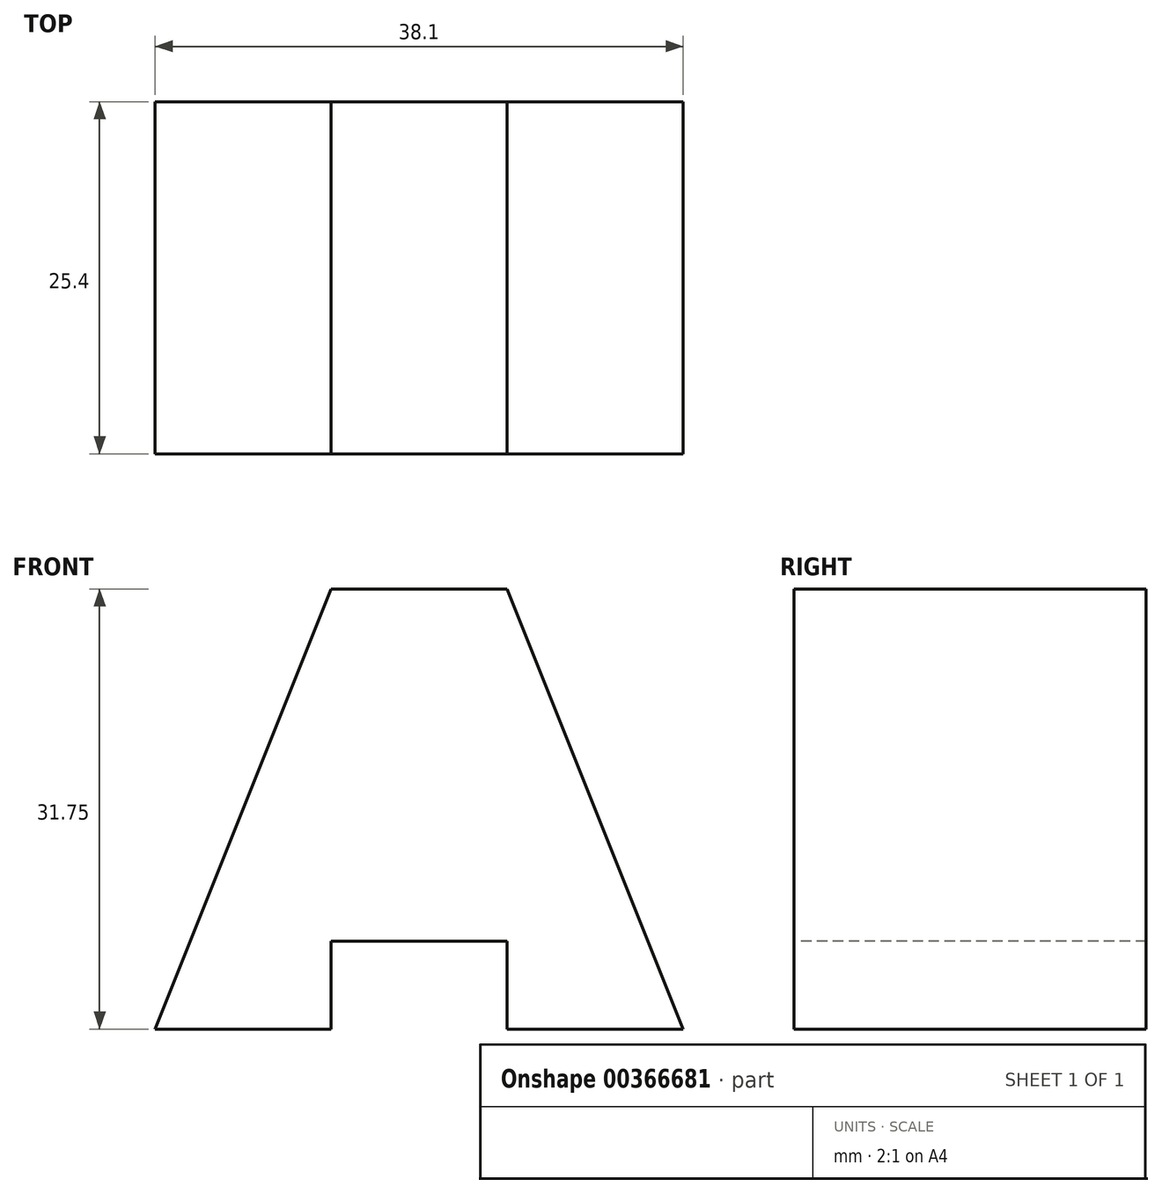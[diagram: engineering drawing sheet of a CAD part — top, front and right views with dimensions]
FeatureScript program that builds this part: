
annotation { "Feature Type Name" : "Feature", "Feature Type Description" : "" }
export const myFeature = defineFeature(function(context is Context, id is Id, definition is map)
    precondition{}
    {
        {
            var Q0;
            Q0=qCreatedBy(makeId("Front.planeOp"),FACE);
            var sketch = newSketch(context, id + "F0", { "sketchPlane" : qUnion([Q0])});
            skLineSegment(sketch, "E0", {"start": v(-39.58, 31.75) * mm, "end": v(-1.48, 31.75) * mm});
            skLineSegment(sketch, "E1", {"start": v(-1.48, 31.75) * mm, "end": v(-1.48, 0) * mm});
            skLineSegment(sketch, "E2", {"start": v(-1.48, 0) * mm, "end": v(-39.58, 0) * mm});
            skLineSegment(sketch, "E3", {"start": v(-39.58, 31.75) * mm, "end": v(-39.58, 0) * mm});
            skSolve(sketch);
        }
        {
            var Q0;
            Q0=makeQuery(id+"F0.imprint","IMPRINT",FACE,{"disambiguationData":[TD([[makeQuery(id+"F0.imprint","IMPRINT",EDGE,{"derivedFrom":sQuery(id+"F0.wireOp",EDGE,"E0")}),-1.0]])]});
            extrude(context, id + "F1", {"entities" : qUnion([Q0]), "depth" : 25.4 * mm});
        }
        {
            var Q0;
            Q0=makeQuery(id+"F1.opExtrude","CAP_FACE",FACE,{"disambiguationData":[OSD([sQuery(id+"F0.wireOp",EDGE,"E0"),sQuery(id+"F0.wireOp",EDGE,"E1"),sQuery(id+"F0.wireOp",EDGE,"E2"),sQuery(id+"F0.wireOp",EDGE,"E3")])],"isStart":false});
            var sketch = newSketch(context, id + "F2", { "sketchPlane" : qUnion([Q0])});
            skLineSegment(sketch, "E4", {"start": v(-14.18, 31.75) * mm, "end": v(-1.48, 0) * mm});
            skLineSegment(sketch, "E5", {"start": v(-26.88, 31.75) * mm, "end": v(-39.58, 0) * mm});
            skSolve(sketch);
        }
        {
            var Q0;
            {var subQ0=sQuery(id+"F2.wireOp",EDGE,"E5");Q0=makeQuery(id+"F2.imprint","IMPRINT",FACE,{"disambiguationData":[TD([[makeQuery(id+"F2.imprint","IMPRINT",EDGE,{"derivedFrom":subQ0}),-1.0]])]});}
            var Q1;
            {var subQ0=sQuery(id+"F2.wireOp",EDGE,"E4");Q1=makeQuery(id+"F2.imprint","IMPRINT",FACE,{"disambiguationData":[TD([[makeQuery(id+"F2.imprint","IMPRINT",EDGE,{"derivedFrom":subQ0}),1.0]])]});}
            extrude(context, id + "F3", {"entities" : qUnion([Q0, Q1]), "operationType" : NewBodyOperationType.REMOVE, "oppositeDirection" : true, "depth" : 25.4 * mm});
        }
        {
            var Q0;
            Q0=makeQuery(id+"F1.opExtrude","CAP_FACE",FACE,{"disambiguationData":[OSD([sQuery(id+"F0.wireOp",EDGE,"E0"),sQuery(id+"F0.wireOp",EDGE,"E1"),sQuery(id+"F0.wireOp",EDGE,"E2"),sQuery(id+"F0.wireOp",EDGE,"E3")])],"isStart":false});
            var sketch = newSketch(context, id + "F4", { "sketchPlane" : qUnion([Q0])});
            skLineSegment(sketch, "E6", {"start": v(-26.88, 0) * mm, "end": v(-26.88, 6.35) * mm});
            skLineSegment(sketch, "E7", {"start": v(-26.88, 6.35) * mm, "end": v(-14.18, 6.35) * mm});
            skLineSegment(sketch, "E8", {"start": v(-14.18, 6.35) * mm, "end": v(-14.18, 0) * mm});
            skSolve(sketch);
        }
        {
            var Q0;
            {var subQ0=sQuery(id+"F4.wireOp",EDGE,"E6");Q0=makeQuery(id+"F4.imprint","IMPRINT",FACE,{"disambiguationData":[TD([[makeQuery(id+"F4.imprint","IMPRINT",EDGE,{"derivedFrom":subQ0}),-1.0]])]});}
            extrude(context, id + "F5", {"entities" : qUnion([Q0]), "operationType" : NewBodyOperationType.REMOVE, "oppositeDirection" : true, "depth" : 25.4 * mm});
        }
    });
